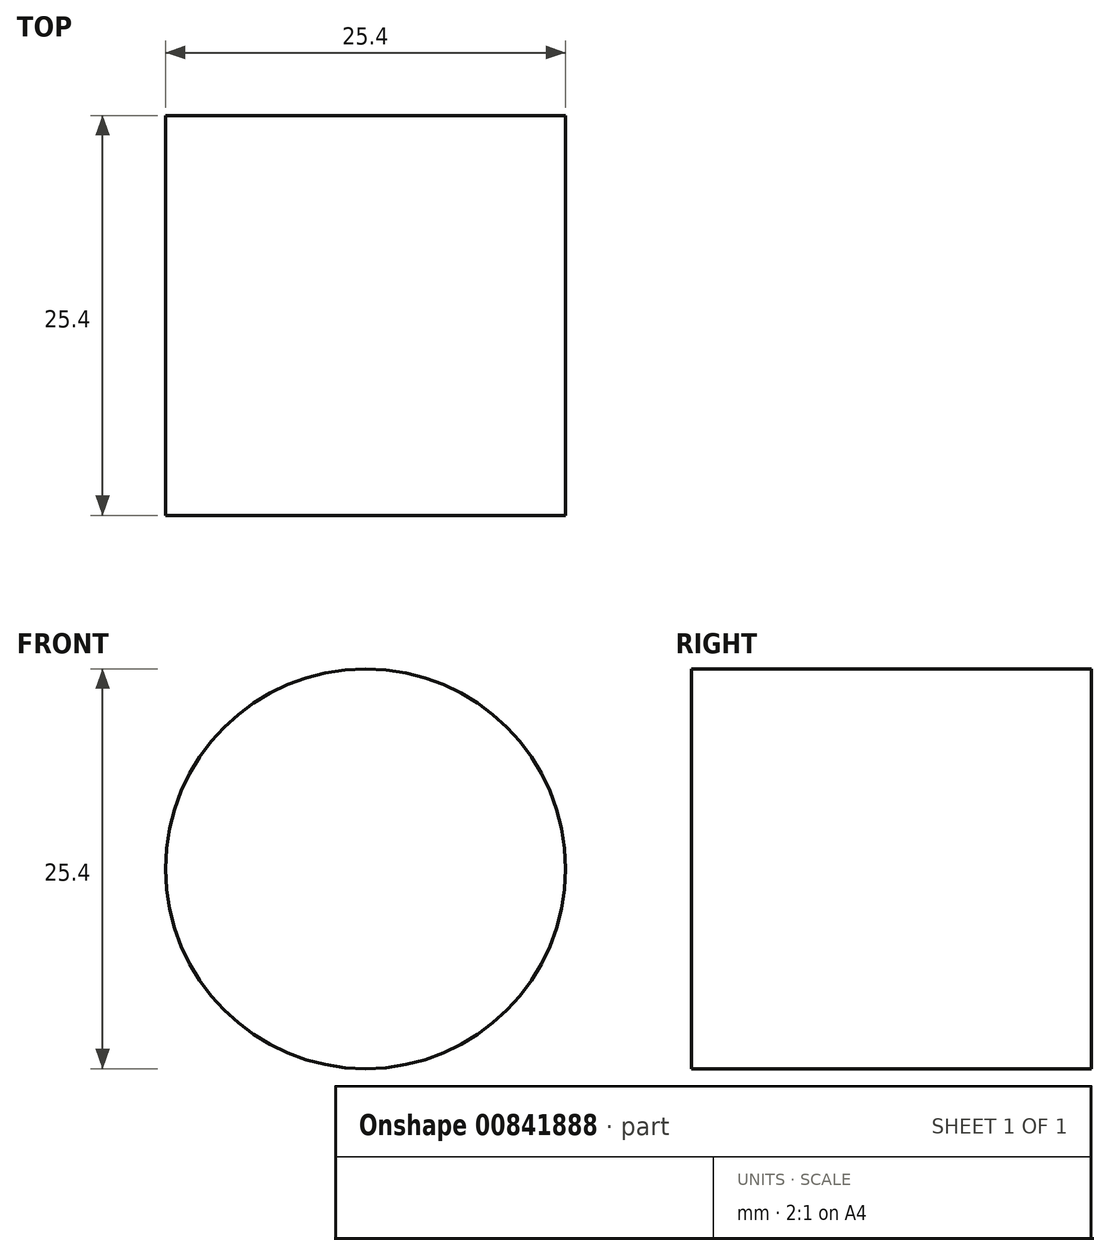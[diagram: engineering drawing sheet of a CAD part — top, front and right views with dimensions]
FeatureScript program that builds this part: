
annotation { "Feature Type Name" : "Feature", "Feature Type Description" : "" }
export const myFeature = defineFeature(function(context is Context, id is Id, definition is map)
    precondition{}
    {
        {
            var Q0;
            Q0=qCreatedBy(makeId("Front.planeOp"),FACE);
            var sketch = newSketch(context, id + "F0", { "sketchPlane" : qUnion([Q0])});
            skCircle(sketch, "E0", {"center": v(-35.06, 0) * mm, "radius": 12.7 * mm});
            skSolve(sketch);
        }
        {
            var Q0;
            Q0=qCreatedBy(makeId("Front.planeOp"),FACE);
            var sketch = newSketch(context, id + "F1", { "sketchPlane" : qUnion([Q0])});
            skSolve(sketch);
        }
        {
            var Q0;
            Q0 = qSketchRegion(id + "F1", true);
            var Q1;
            Q1=makeQuery(id+"F0.imprint","IMPRINT",FACE,{"disambiguationData":[TD([[makeQuery(id+"F0.imprint","IMPRINT",EDGE,{"derivedFrom":sQuery(id+"F0.wireOp",EDGE,"E0")}),1.0]])]});
            extrude(context, id + "F2", {"entities" : qUnion([Q0, Q1]), "depth" : 25.4 * mm, "offsetDistance" : 25.4 * mm});
        }
    });
